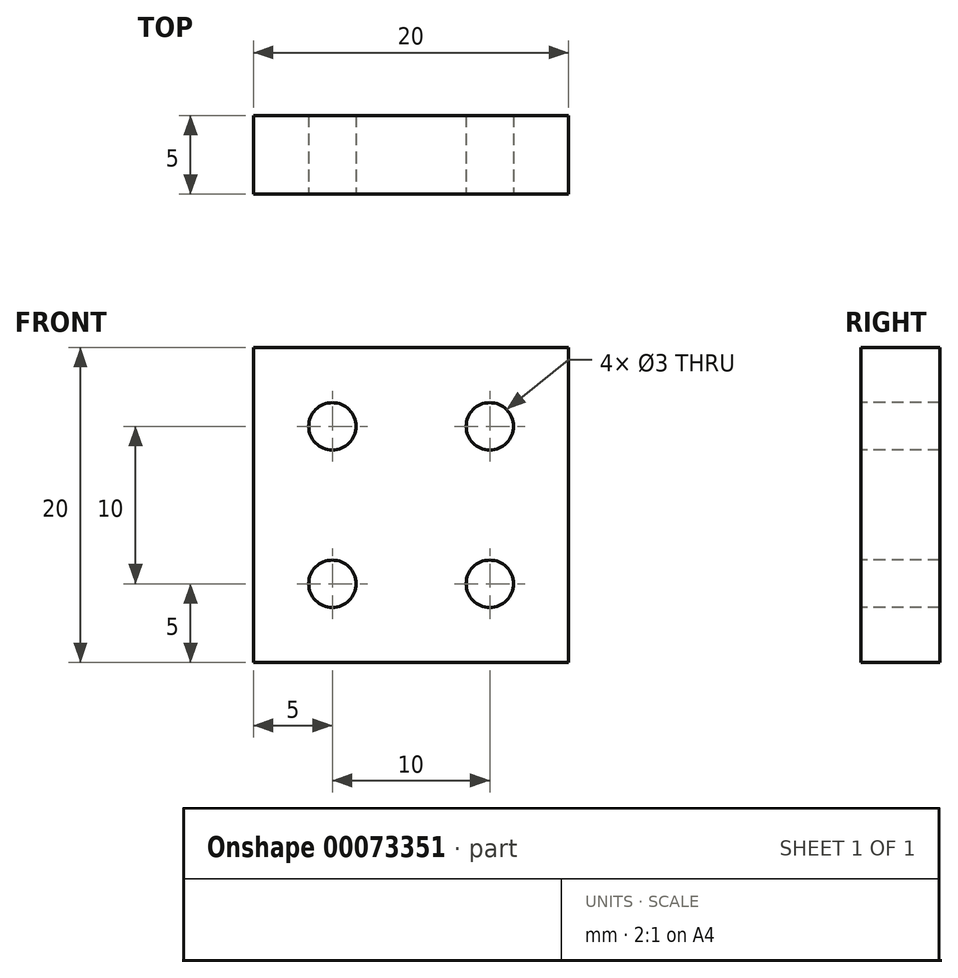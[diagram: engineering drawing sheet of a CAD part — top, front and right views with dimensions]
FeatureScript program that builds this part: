
annotation { "Feature Type Name" : "Feature", "Feature Type Description" : "" }
export const myFeature = defineFeature(function(context is Context, id is Id, definition is map)
    precondition{}
    {
        {
            var Q0;
            Q0=qCreatedBy(makeId("Front.planeOp"),FACE);
            var sketch = newSketch(context, id + "F0", { "sketchPlane" : qUnion([Q0])});
            skLineSegment(sketch, "E0.bottom", {"start": v(-10, 10) * mm, "end": v(10, 10) * mm});
            skLineSegment(sketch, "E0.top", {"start": v(-10, -10) * mm, "end": v(10, -10) * mm});
            skLineSegment(sketch, "E0.left", {"start": v(-10, 10) * mm, "end": v(-10, -10) * mm});
            skLineSegment(sketch, "E0.right", {"start": v(10, 10) * mm, "end": v(10, -10) * mm});
            skLineSegment(sketch, "E1", {"start": v(-10, 10) * mm, "end": v(10, -10) * mm, "construction": true});
            skPoint(sketch, "E2", {"position": v(0, 0) * mm});
            skSolve(sketch);
        }
        {
            var Q0;
            Q0=makeQuery(id+"F0.imprint","IMPRINT",FACE,{"disambiguationData":[TD([[makeQuery(id+"F0.imprint","IMPRINT",EDGE,{"derivedFrom":sQuery(id+"F0.wireOp",EDGE,"E0.bottom")}),-1.0]])]});
            extrude(context, id + "F1", {"entities" : qUnion([Q0]), "depth" : 5 * mm, "offsetDistance" : 25 * mm, "symmetric" : true});
        }
        {
            var Q0;
            Q0=makeQuery(id+"F1.opExtrude","CAP_FACE",FACE,{"disambiguationData":[OSD([sQuery(id+"F0.wireOp",EDGE,"E0.bottom"),sQuery(id+"F0.wireOp",EDGE,"E0.top"),sQuery(id+"F0.wireOp",EDGE,"E0.left"),sQuery(id+"F0.wireOp",EDGE,"E0.right")])],"isStart":false});
            var sketch = newSketch(context, id + "F2", { "sketchPlane" : qUnion([Q0])});
            skLineSegment(sketch, "E3.bottom", {"start": v(-5, 5) * mm, "end": v(5, 5) * mm});
            skLineSegment(sketch, "E3.top", {"start": v(-5, -5) * mm, "end": v(5, -5) * mm});
            skLineSegment(sketch, "E3.left", {"start": v(-5, 5) * mm, "end": v(-5, -5) * mm});
            skLineSegment(sketch, "E3.right", {"start": v(5, 5) * mm, "end": v(5, -5) * mm});
            skLineSegment(sketch, "E4", {"start": v(-5, 5) * mm, "end": v(5, -5) * mm, "construction": true});
            skPoint(sketch, "E5", {"position": v(0, 0) * mm});
            skSolve(sketch);
        }
        {
            var Q0;
            Q0=sQuery(id+"F2.wireOp",VERTEX,"E3.bottom.start");
            var Q1;
            Q1=sQuery(id+"F2.wireOp",VERTEX,"E3.bottom.end");
            var Q2;
            Q2=sQuery(id+"F2.wireOp",VERTEX,"E3.top.end");
            var Q3;
            Q3=sQuery(id+"F2.wireOp",VERTEX,"E3.top.start");
            var Q4;
            Q4=makeQuery(id+"F1.opExtrude","SWEPT_BODY",BODY,{"disambiguationData":[OSD([sQuery(id+"F0.wireOp",EDGE,"E0.bottom"),sQuery(id+"F0.wireOp",EDGE,"E0.top"),sQuery(id+"F0.wireOp",EDGE,"E0.left"),sQuery(id+"F0.wireOp",EDGE,"E0.right")])]});
            hole(context, id + "F3", {"style" : HoleStyle.SIMPLE, "endStyle" : HoleEndStyle.THROUGH, "holeDiameter" : 3 * mm, "majorDiameter" : 5 * mm, "tappedDepth" : 12 * mm, "tapClearance" : 3, "locations" : qUnion([Q0, Q1, Q2, Q3]), "scope" : qUnion([Q4])});
        }
    });
